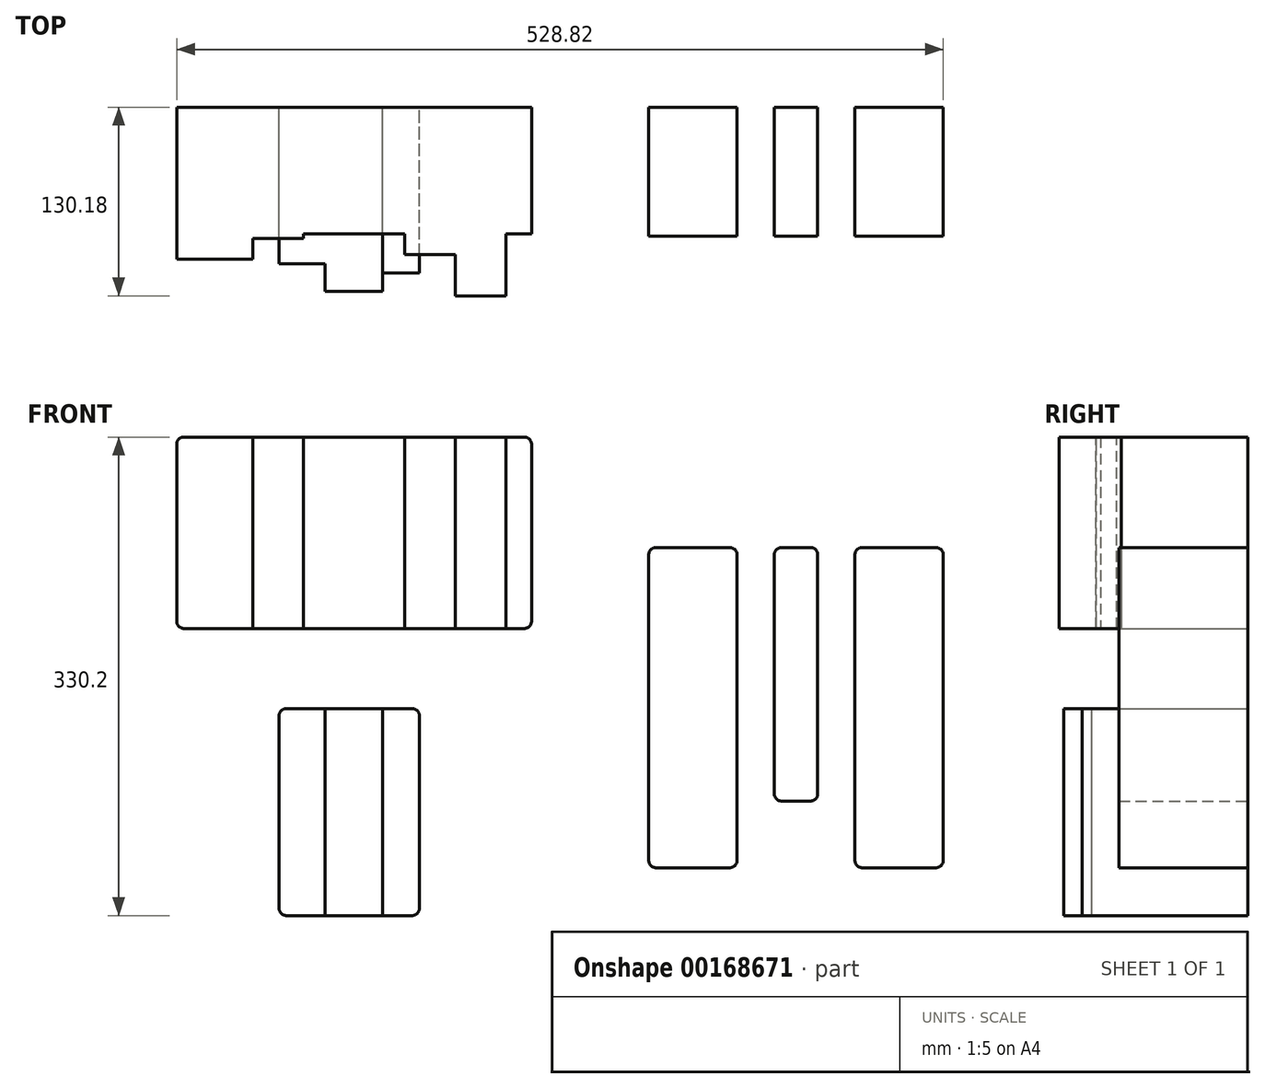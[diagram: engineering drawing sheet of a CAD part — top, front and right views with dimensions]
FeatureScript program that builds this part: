
annotation { "Feature Type Name" : "Feature", "Feature Type Description" : "" }
export const myFeature = defineFeature(function(context is Context, id is Id, definition is map)
    precondition{}
    {
        {
            var Q0;
            Q0=qCreatedBy(makeId("Front.planeOp"),FACE);
            var sketch = newSketch(context, id + "F0", { "sketchPlane" : qUnion([Q0])});
            skLineSegment(sketch, "E0.bottom", {"start": v(401.82, -139.7) * mm, "end": v(462.78, -139.7) * mm});
            skLineSegment(sketch, "E0.top", {"start": v(401.82, -360.68) * mm, "end": v(462.78, -360.68) * mm});
            skLineSegment(sketch, "E0.left", {"start": v(401.82, -139.7) * mm, "end": v(401.82, -360.68) * mm});
            skLineSegment(sketch, "E0.right", {"start": v(462.78, -139.7) * mm, "end": v(462.78, -360.68) * mm});
            skLineSegment(sketch, "E1.bottom", {"start": v(544.06, -139.7) * mm, "end": v(605.02, -139.7) * mm});
            skLineSegment(sketch, "E1.top", {"start": v(544.06, -360.68) * mm, "end": v(605.02, -360.68) * mm});
            skLineSegment(sketch, "E1.left", {"start": v(544.06, -139.7) * mm, "end": v(544.06, -360.68) * mm});
            skLineSegment(sketch, "E1.right", {"start": v(605.02, -139.7) * mm, "end": v(605.02, -360.68) * mm});
            skLineSegment(sketch, "E2.bottom", {"start": v(488.43, -139.7) * mm, "end": v(518.4, -139.7) * mm});
            skLineSegment(sketch, "E2.top", {"start": v(488.43, -314.7) * mm, "end": v(518.4, -314.7) * mm});
            skLineSegment(sketch, "E2.left", {"start": v(488.43, -139.7) * mm, "end": v(488.43, -314.7) * mm});
            skLineSegment(sketch, "E2.right", {"start": v(518.4, -139.7) * mm, "end": v(518.4, -314.7) * mm});
            skLineSegment(sketch, "E3.bottom", {"start": v(0, 0) * mm, "end": v(736.6, 0) * mm, "construction": true});
            skLineSegment(sketch, "E3.top", {"start": v(0, -457.2) * mm, "end": v(736.6, -457.2) * mm, "construction": true});
            skLineSegment(sketch, "E3.left", {"start": v(0, 0) * mm, "end": v(0, -457.2) * mm, "construction": true});
            skLineSegment(sketch, "E3.right", {"start": v(736.6, 0) * mm, "end": v(736.6, -457.2) * mm, "construction": true});
            skLineSegment(sketch, "E4.right", {"start": v(128.59, -195.58) * mm, "end": v(128.59, -63.5) * mm});
            skLineSegment(sketch, "E5.bottom", {"start": v(128.59, -63.5) * mm, "end": v(163.51, -63.5) * mm});
            skLineSegment(sketch, "E5.top", {"start": v(128.59, -195.58) * mm, "end": v(163.51, -195.58) * mm});
            skLineSegment(sketch, "E5.left", {"start": v(128.59, -63.5) * mm, "end": v(128.59, -195.58) * mm});
            skLineSegment(sketch, "E5.right", {"start": v(163.51, -63.5) * mm, "end": v(163.51, -195.58) * mm});
            skLineSegment(sketch, "E6.bottom", {"start": v(163.51, -63.5) * mm, "end": v(233.36, -63.5) * mm});
            skLineSegment(sketch, "E6.top", {"start": v(163.51, -195.58) * mm, "end": v(233.36, -195.58) * mm});
            skLineSegment(sketch, "E6.right", {"start": v(233.36, -63.5) * mm, "end": v(233.36, -195.58) * mm});
            skLineSegment(sketch, "E7.bottom", {"start": v(233.36, -63.5) * mm, "end": v(268.29, -63.5) * mm});
            skLineSegment(sketch, "E7.top", {"start": v(233.36, -195.58) * mm, "end": v(268.29, -195.58) * mm});
            skLineSegment(sketch, "E7.right", {"start": v(268.29, -63.5) * mm, "end": v(268.29, -195.58) * mm});
            skLineSegment(sketch, "E8.bottom", {"start": v(268.29, -63.5) * mm, "end": v(303.21, -63.5) * mm});
            skLineSegment(sketch, "E8.top", {"start": v(268.29, -195.58) * mm, "end": v(303.21, -195.58) * mm});
            skLineSegment(sketch, "E8.right", {"start": v(303.21, -63.5) * mm, "end": v(303.21, -195.58) * mm});
            skLineSegment(sketch, "E9.bottom", {"start": v(303.21, -63.5) * mm, "end": v(321, -63.5) * mm});
            skLineSegment(sketch, "E9.top", {"start": v(303.21, -195.58) * mm, "end": v(321, -195.58) * mm});
            skLineSegment(sketch, "E9.right", {"start": v(321, -63.5) * mm, "end": v(321, -195.58) * mm});
            skPoint(sketch, "E10", {"position": v(50.8, -50.8) * mm});
            skLineSegment(sketch, "E11.bottom", {"start": v(128.59, -63.5) * mm, "end": v(76.2, -63.5) * mm});
            skLineSegment(sketch, "E11.top", {"start": v(128.59, -195.58) * mm, "end": v(76.2, -195.58) * mm});
            skLineSegment(sketch, "E11.right", {"start": v(76.2, -63.5) * mm, "end": v(76.2, -195.58) * mm});
            skPoint(sketch, "E12", {"position": v(685.8, -50.8) * mm});
            skLineSegment(sketch, "E13.bottom", {"start": v(146.84, -250.83) * mm, "end": v(178.59, -250.83) * mm});
            skLineSegment(sketch, "E13.top", {"start": v(146.84, -393.7) * mm, "end": v(178.59, -393.7) * mm});
            skLineSegment(sketch, "E13.left", {"start": v(146.84, -250.83) * mm, "end": v(146.84, -393.7) * mm});
            skLineSegment(sketch, "E13.right", {"start": v(178.59, -250.83) * mm, "end": v(178.59, -393.7) * mm});
            skLineSegment(sketch, "E14.bottom", {"start": v(178.59, -250.83) * mm, "end": v(218.27, -250.83) * mm});
            skLineSegment(sketch, "E14.top", {"start": v(178.59, -393.7) * mm, "end": v(218.27, -393.7) * mm});
            skLineSegment(sketch, "E14.right", {"start": v(218.27, -250.83) * mm, "end": v(218.27, -393.7) * mm});
            skLineSegment(sketch, "E15.bottom", {"start": v(218.27, -250.83) * mm, "end": v(243.67, -250.83) * mm});
            skLineSegment(sketch, "E15.top", {"start": v(218.27, -393.7) * mm, "end": v(243.67, -393.7) * mm});
            skLineSegment(sketch, "E15.right", {"start": v(243.67, -250.83) * mm, "end": v(243.67, -393.7) * mm});
            skPoint(sketch, "E16", {"position": v(50.8, -406.4) * mm});
            skPoint(sketch, "E17", {"position": v(685.8, -406.4) * mm});
            skSolve(sketch);
        }
        {
            var Q0;
            Q0=makeQuery(id+"F0.imprint","IMPRINT",FACE,{"disambiguationData":[TD([[makeQuery(id+"F0.imprint","IMPRINT",EDGE,{"derivedFrom":sQuery(id+"F0.wireOp",EDGE,"E0.bottom")}),-1.0]])]});
            var Q1;
            Q1=makeQuery(id+"F0.imprint","IMPRINT",FACE,{"disambiguationData":[TD([[makeQuery(id+"F0.imprint","IMPRINT",EDGE,{"derivedFrom":sQuery(id+"F0.wireOp",EDGE,"E1.bottom")}),-1.0]])]});
            var Q2;
            Q2=makeQuery(id+"F0.imprint","IMPRINT",FACE,{"disambiguationData":[TD([[makeQuery(id+"F0.imprint","IMPRINT",EDGE,{"derivedFrom":sQuery(id+"F0.wireOp",EDGE,"E2.bottom")}),-1.0]])]});
            extrude(context, id + "F1", {"entities" : qUnion([Q0, Q1, Q2]), "depth" : 88.9 * mm});
        }
        {
            var Q0;
            Q0=makeQuery(id+"F1.opExtrude","SWEPT_EDGE",EDGE,{"disambiguationData":[OSD([sQuery(id+"F0.wireOp",EDGE,"E0.bottom"),sQuery(id+"F0.wireOp",EDGE,"E0.right")])]});
            var Q1;
            Q1=makeQuery(id+"F1.opExtrude","SWEPT_EDGE",EDGE,{"disambiguationData":[OSD([sQuery(id+"F0.wireOp",EDGE,"E2.bottom"),sQuery(id+"F0.wireOp",EDGE,"E2.right")])]});
            var Q2;
            Q2=makeQuery(id+"F1.opExtrude","SWEPT_EDGE",EDGE,{"disambiguationData":[OSD([sQuery(id+"F0.wireOp",EDGE,"E1.bottom"),sQuery(id+"F0.wireOp",EDGE,"E1.right")])]});
            var Q3;
            Q3=makeQuery(id+"F1.opExtrude","SWEPT_EDGE",EDGE,{"disambiguationData":[OSD([sQuery(id+"F0.wireOp",EDGE,"E1.bottom"),sQuery(id+"F0.wireOp",EDGE,"E1.left")])]});
            var Q4;
            Q4=makeQuery(id+"F1.opExtrude","SWEPT_EDGE",EDGE,{"disambiguationData":[OSD([sQuery(id+"F0.wireOp",EDGE,"E0.bottom"),sQuery(id+"F0.wireOp",EDGE,"E0.left")])]});
            var Q5;
            Q5=makeQuery(id+"F1.opExtrude","SWEPT_EDGE",EDGE,{"disambiguationData":[OSD([sQuery(id+"F0.wireOp",EDGE,"E0.top"),sQuery(id+"F0.wireOp",EDGE,"E0.left")])]});
            var Q6;
            Q6=makeQuery(id+"F1.opExtrude","SWEPT_EDGE",EDGE,{"disambiguationData":[OSD([sQuery(id+"F0.wireOp",EDGE,"E2.top"),sQuery(id+"F0.wireOp",EDGE,"E2.left")])]});
            var Q7;
            Q7=makeQuery(id+"F1.opExtrude","SWEPT_EDGE",EDGE,{"disambiguationData":[OSD([sQuery(id+"F0.wireOp",EDGE,"E1.top"),sQuery(id+"F0.wireOp",EDGE,"E1.left")])]});
            var Q8;
            Q8=makeQuery(id+"F1.opExtrude","SWEPT_EDGE",EDGE,{"disambiguationData":[OSD([sQuery(id+"F0.wireOp",EDGE,"E0.top"),sQuery(id+"F0.wireOp",EDGE,"E0.right")])]});
            var Q9;
            Q9=makeQuery(id+"F1.opExtrude","SWEPT_EDGE",EDGE,{"disambiguationData":[OSD([sQuery(id+"F0.wireOp",EDGE,"E2.top"),sQuery(id+"F0.wireOp",EDGE,"E2.right")])]});
            var Q10;
            Q10=makeQuery(id+"F1.opExtrude","SWEPT_EDGE",EDGE,{"disambiguationData":[OSD([sQuery(id+"F0.wireOp",EDGE,"E1.top"),sQuery(id+"F0.wireOp",EDGE,"E1.right")])]});
            fillet(context, id + "F2", {"entities" : qUnion([Q0, Q1, Q2, Q3, Q4, Q5, Q6, Q7, Q8, Q9, Q10]), "radius" : 5.08 * mm, "tangentPropagation" : true, "allowEdgeOverflow" : false});
        }
        {
            var Q0;
            Q0=makeQuery(id+"F1.opExtrude","SWEPT_EDGE",EDGE,{"disambiguationData":[OSD([sQuery(id+"F0.wireOp",EDGE,"E2.bottom"),sQuery(id+"F0.wireOp",EDGE,"E2.left")])]});
            var Q1;
            Q1=makeQuery(id+"FXifytqj1vpHj8I_2.opExtrude","SWEPT_EDGE",EDGE,{"disambiguationData":[OSD([sQuery(id+"F0.wireOp",EDGE,"VYxTvCZB-CYbp-Cyqk-qKJR-zw5bBLdlwLOv.top"),sQuery(id+"F0.wireOp",EDGE,"VYxTvCZB-CYbp-Cyqk-qKJR-zw5bBLdlwLOv.left")])]});
            var Q2;
            Q2=makeQuery(id+"FXifytqj1vpHj8I_2.opExtrude","SWEPT_EDGE",EDGE,{"disambiguationData":[OSD([sQuery(id+"F0.wireOp",EDGE,"VYxTvCZB-CYbp-Cyqk-qKJR-zw5bBLdlwLOv.bottom"),sQuery(id+"F0.wireOp",EDGE,"VYxTvCZB-CYbp-Cyqk-qKJR-zw5bBLdlwLOv.left")])]});
            var Q3;
            Q3=makeQuery(id+"FB6OAgb9by0tff1_1.opExtrude","SWEPT_EDGE",EDGE,{"disambiguationData":[OSD([sQuery(id+"F0.wireOp",EDGE,"04hokktK-nRdH-FnVl-lkE3-cBnQYboMP6h8.top"),sQuery(id+"F0.wireOp",EDGE,"04hokktK-nRdH-FnVl-lkE3-cBnQYboMP6h8.right")])]});
            var Q4;
            Q4=makeQuery(id+"FXifytqj1vpHj8I_2.opExtrude","SWEPT_EDGE",EDGE,{"disambiguationData":[OSD([sQuery(id+"F0.wireOp",EDGE,"VYxTvCZB-CYbp-Cyqk-qKJR-zw5bBLdlwLOv.bottom"),sQuery(id+"F0.wireOp",EDGE,"VYxTvCZB-CYbp-Cyqk-qKJR-zw5bBLdlwLOv.right")])]});
            var Q5;
            Q5=makeQuery(id+"FB6OAgb9by0tff1_1.opExtrude","SWEPT_EDGE",EDGE,{"disambiguationData":[OSD([sQuery(id+"F0.wireOp",EDGE,"04hokktK-nRdH-FnVl-lkE3-cBnQYboMP6h8.bottom"),sQuery(id+"F0.wireOp",EDGE,"04hokktK-nRdH-FnVl-lkE3-cBnQYboMP6h8.right")])]});
            var Q6;
            Q6=makeQuery(id+"FXifytqj1vpHj8I_2.opExtrude","SWEPT_EDGE",EDGE,{"disambiguationData":[OSD([sQuery(id+"F0.wireOp",EDGE,"VYxTvCZB-CYbp-Cyqk-qKJR-zw5bBLdlwLOv.top"),sQuery(id+"F0.wireOp",EDGE,"04hokktK-nRdH-FnVl-lkE3-cBnQYboMP6h8.bottom"),sQuery(id+"F0.wireOp",EDGE,"04hokktK-nRdH-FnVl-lkE3-cBnQYboMP6h8.left")])]});
            fillet(context, id + "F3", {"entities" : qUnion([Q0, Q1, Q2, Q3, Q4, Q5, Q6]), "radius" : 5.08 * mm, "tangentPropagation" : true, "allowEdgeOverflow" : false});
        }
        {
            var Q0;
            Q0=makeQuery(id+"F0.imprint","IMPRINT",FACE,{"disambiguationData":[TD([[makeQuery(id+"F0.imprint","IMPRINT",EDGE,{"derivedFrom":sQuery(id+"F0.wireOp",EDGE,"E11.bottom")}),1.0]])]});
            extrude(context, id + "F4", {"entities" : qUnion([Q0]), "depth" : 104.77 * mm});
        }
        {
            var Q0;
            Q0=makeQuery(id+"F0.imprint","IMPRINT",FACE,{"disambiguationData":[TD([[makeQuery(id+"F0.imprint","IMPRINT",EDGE,{"derivedFrom":sQuery(id+"F0.wireOp",EDGE,"E5.bottom")}),-1.0]])]});
            extrude(context, id + "F5", {"entities" : qUnion([Q0]), "operationType" : NewBodyOperationType.ADD, "depth" : 90.5 * mm});
        }
        {
            var Q0;
            Q0=makeQuery(id+"F0.imprint","IMPRINT",FACE,{"disambiguationData":[TD([[makeQuery(id+"F0.imprint","IMPRINT",EDGE,{"derivedFrom":sQuery(id+"F0.wireOp",EDGE,"E6.bottom")}),-1.0]])]});
            extrude(context, id + "F6", {"entities" : qUnion([Q0]), "operationType" : NewBodyOperationType.ADD, "depth" : 87.33 * mm});
        }
        {
            var Q0;
            Q0=makeQuery(id+"F0.imprint","IMPRINT",FACE,{"disambiguationData":[TD([[makeQuery(id+"F0.imprint","IMPRINT",EDGE,{"derivedFrom":sQuery(id+"F0.wireOp",EDGE,"E7.bottom")}),-1.0]])]});
            extrude(context, id + "F7", {"entities" : qUnion([Q0]), "operationType" : NewBodyOperationType.ADD, "depth" : 101.6 * mm});
        }
        {
            var Q0;
            Q0=makeQuery(id+"F0.imprint","IMPRINT",FACE,{"disambiguationData":[TD([[makeQuery(id+"F0.imprint","IMPRINT",EDGE,{"derivedFrom":sQuery(id+"F0.wireOp",EDGE,"E8.bottom")}),-1.0]])]});
            extrude(context, id + "F8", {"entities" : qUnion([Q0]), "operationType" : NewBodyOperationType.ADD, "depth" : 130.17 * mm});
        }
        {
            var Q0;
            Q0=makeQuery(id+"F0.imprint","IMPRINT",FACE,{"disambiguationData":[TD([[makeQuery(id+"F0.imprint","IMPRINT",EDGE,{"derivedFrom":sQuery(id+"F0.wireOp",EDGE,"E9.bottom")}),-1.0]])]});
            extrude(context, id + "F9", {"entities" : qUnion([Q0]), "operationType" : NewBodyOperationType.ADD, "depth" : 87.33 * mm});
        }
        {
            var Q0;
            Q0=makeQuery(id+"F0.imprint","IMPRINT",FACE,{"disambiguationData":[TD([[makeQuery(id+"F0.imprint","IMPRINT",EDGE,{"derivedFrom":sQuery(id+"F0.wireOp",EDGE,"E13.bottom")}),-1.0]])]});
            extrude(context, id + "F10", {"entities" : qUnion([Q0]), "depth" : 107.95 * mm});
        }
        {
            var Q0;
            Q0=makeQuery(id+"F0.imprint","IMPRINT",FACE,{"disambiguationData":[TD([[makeQuery(id+"F0.imprint","IMPRINT",EDGE,{"derivedFrom":sQuery(id+"F0.wireOp",EDGE,"E14.bottom")}),-1.0]])]});
            extrude(context, id + "F11", {"entities" : qUnion([Q0]), "operationType" : NewBodyOperationType.ADD, "depth" : 127 * mm});
        }
        {
            var Q0;
            Q0=makeQuery(id+"F0.imprint","IMPRINT",FACE,{"disambiguationData":[TD([[makeQuery(id+"F0.imprint","IMPRINT",EDGE,{"derivedFrom":sQuery(id+"F0.wireOp",EDGE,"E15.bottom")}),-1.0]])]});
            extrude(context, id + "F12", {"entities" : qUnion([Q0]), "depth" : 114.3 * mm});
        }
        {
            var Q0;
            Q0=makeQuery(id+"F9.opExtrude","SWEPT_EDGE",EDGE,{"disambiguationData":[OSD([sQuery(id+"F0.wireOp",EDGE,"E9.bottom"),sQuery(id+"F0.wireOp",EDGE,"E9.right")])]});
            var Q1;
            Q1=makeQuery(id+"F4.opExtrude","SWEPT_EDGE",EDGE,{"disambiguationData":[OSD([sQuery(id+"F0.wireOp",EDGE,"E11.bottom"),sQuery(id+"F0.wireOp",EDGE,"E11.right")])]});
            var Q2;
            Q2=makeQuery(id+"F9.opExtrude","SWEPT_EDGE",EDGE,{"disambiguationData":[OSD([sQuery(id+"F0.wireOp",EDGE,"E9.top"),sQuery(id+"F0.wireOp",EDGE,"E9.right")])]});
            var Q3;
            Q3=makeQuery(id+"F4.opExtrude","SWEPT_EDGE",EDGE,{"disambiguationData":[OSD([sQuery(id+"F0.wireOp",EDGE,"E11.top"),sQuery(id+"F0.wireOp",EDGE,"E11.right")])]});
            var Q4;
            Q4=makeQuery(id+"F10.opExtrude","SWEPT_EDGE",EDGE,{"disambiguationData":[OSD([sQuery(id+"F0.wireOp",EDGE,"E13.bottom"),sQuery(id+"F0.wireOp",EDGE,"E13.left")])]});
            var Q5;
            Q5=makeQuery(id+"F10.opExtrude","SWEPT_EDGE",EDGE,{"disambiguationData":[OSD([sQuery(id+"F0.wireOp",EDGE,"E13.top"),sQuery(id+"F0.wireOp",EDGE,"E13.left")])]});
            var Q6;
            Q6=makeQuery(id+"F12.opExtrude","SWEPT_EDGE",EDGE,{"disambiguationData":[OSD([sQuery(id+"F0.wireOp",EDGE,"E15.bottom"),sQuery(id+"F0.wireOp",EDGE,"E15.right")])]});
            var Q7;
            Q7=makeQuery(id+"F12.opExtrude","SWEPT_EDGE",EDGE,{"disambiguationData":[OSD([sQuery(id+"F0.wireOp",EDGE,"E15.top"),sQuery(id+"F0.wireOp",EDGE,"E15.right")])]});
            fillet(context, id + "F13", {"entities" : qUnion([Q0, Q1, Q2, Q3, Q4, Q5, Q6, Q7]), "radius" : 5.08 * mm, "tangentPropagation" : true, "allowEdgeOverflow" : false});
        }
    });
